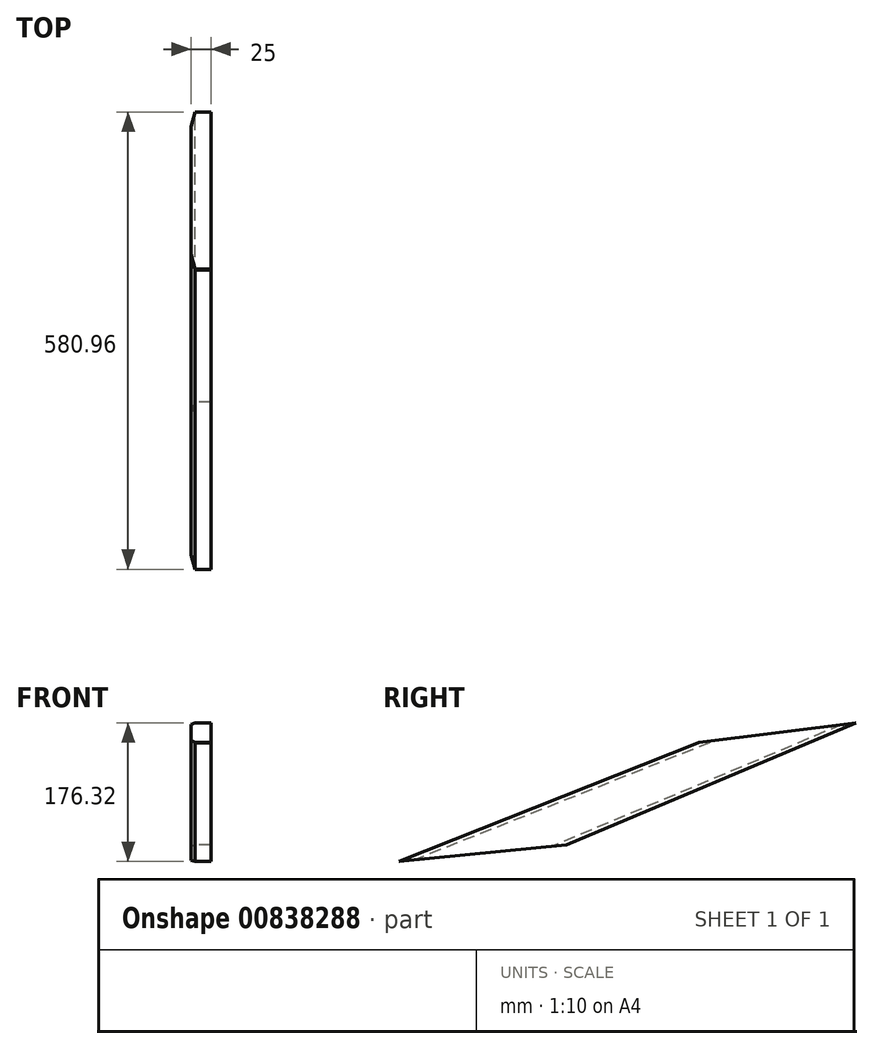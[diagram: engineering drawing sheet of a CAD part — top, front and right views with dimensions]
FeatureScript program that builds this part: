
annotation { "Feature Type Name" : "Feature", "Feature Type Description" : "" }
export const myFeature = defineFeature(function(context is Context, id is Id, definition is map)
    precondition{}
    {
        {
            var Q0;
            Q0=qCreatedBy(makeId("Right.planeOp"),FACE);
            var sketch = newSketch(context, id + "F0", { "sketchPlane" : qUnion([Q0])});
            skLineSegment(sketch, "E0", {"start": v(0, 0) * mm, "end": v(-368.24, -154.9) * mm});
            skLineSegment(sketch, "E1", {"start": v(-368.24, -154.9) * mm, "end": v(-580.96, -176.32) * mm});
            skLineSegment(sketch, "E2", {"start": v(-580.96, -176.32) * mm, "end": v(-200.16, -25.16) * mm});
            skLineSegment(sketch, "E3", {"start": v(-200.16, -25.16) * mm, "end": v(0, 0) * mm});
            skSolve(sketch);
        }
        {
            var Q0;
            Q0 = qSketchRegion(id + "F0", true);
            extrude(context, id + "F1", {"entities" : qUnion([Q0]), "depth" : 25 * mm, "offsetDistance" : 25 * mm});
        }
        {
            var Q0;
            Q0=makeQuery(id+"F1.opExtrude","SWEPT_EDGE",EDGE,{"disambiguationData":[OSD([sQuery(id+"F0.wireOp",EDGE,"E2"),sQuery(id+"F0.wireOp",EDGE,"E3")])]});
            var Q1;
            Q1=makeQuery(id+"F1.opExtrude","CAP_EDGE",EDGE,{"disambiguationData":[OSD([sQuery(id+"F0.wireOp",EDGE,"E0")])],"isStart":true});
            var Q2;
            Q2=makeQuery(id+"F1.opExtrude","CAP_EDGE",EDGE,{"disambiguationData":[OSD([sQuery(id+"F0.wireOp",EDGE,"E2")])],"isStart":true});
            chamfer(context, id + "F2", {"entities" : qUnion([Q0, Q1, Q2]), "width" : 5 * mm, "tangentPropagation" : true});
        }
    });
